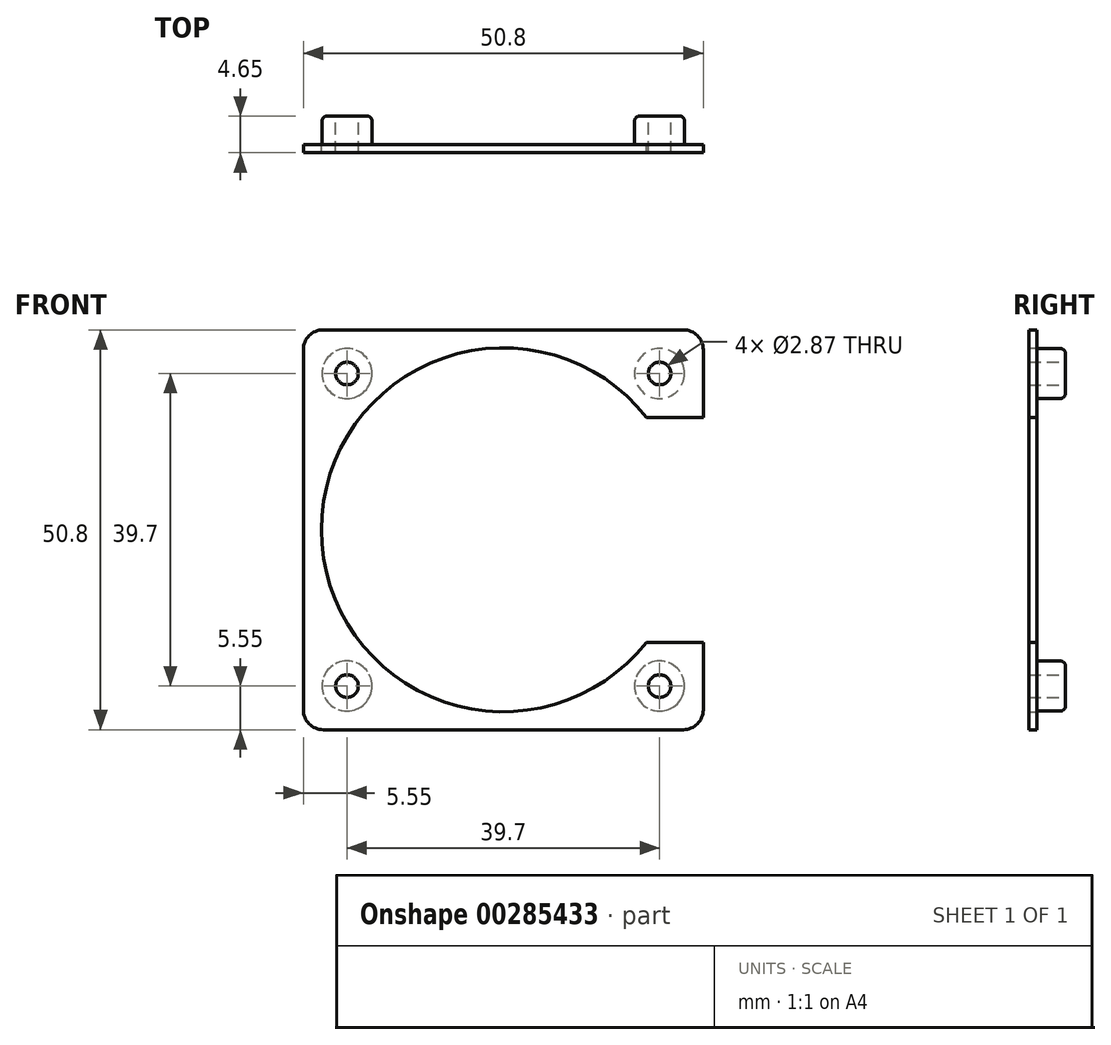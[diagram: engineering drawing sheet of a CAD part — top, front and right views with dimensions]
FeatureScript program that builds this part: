
annotation { "Feature Type Name" : "Feature", "Feature Type Description" : "" }
export const myFeature = defineFeature(function(context is Context, id is Id, definition is map)
    precondition{}
    {
        {
            var Q0;
            Q0=qCreatedBy(makeId("Front.planeOp"),FACE);
            var sketch = newSketch(context, id + "F0", { "sketchPlane" : qUnion([Q0])});
            skLineSegment(sketch, "E0.bottom", {"start": v(2.54, 0) * mm, "end": v(48.26, 0) * mm});
            skLineSegment(sketch, "E0.top", {"start": v(2.54, 50.8) * mm, "end": v(48.26, 50.8) * mm});
            skLineSegment(sketch, "E0.left", {"start": v(0, 2.54) * mm, "end": v(0, 48.26) * mm});
            skLineSegment(sketch, "E0.right", {"start": v(50.8, 2.54) * mm, "end": v(50.8, 11.11) * mm});
            skLineSegment(sketch, "E1", {"start": v(50.8, 39.69) * mm, "end": v(43.57, 39.69) * mm});
            skLineSegment(sketch, "E2", {"start": v(50.8, 11.11) * mm, "end": v(43.57, 11.11) * mm});
            skLineSegment(sketch, "E3", {"start": v(25.4, 50.8) * mm, "end": v(25.4, 0) * mm, "construction": true});
            skLineSegment(sketch, "E4", {"start": v(0, 25.4) * mm, "end": v(50.8, 25.4) * mm, "construction": true});
            skLineSegment(sketch, "E5", {"start": v(43.57, 39.69) * mm, "end": v(43.57, 11.11) * mm, "construction": true});
            skPoint(sketch, "E6", {"position": v(43.57, 25.4) * mm});
            skArc(sketch, "E7", {"start": v(43.57, 39.69) * mm, "mid": v(2.29, 25.4) * mm, "end": v(43.57, 11.11) * mm});
            skLineSegment(sketch, "E8.trimOffspring", {"start": v(50.8, 39.69) * mm, "end": v(50.8, 48.26) * mm});
            skPoint(sketch, "E9.visualSharp", {"position": v(0, 50.8) * mm});
            skArc(sketch, "E9.filletArc", {"start": v(2.54, 50.8) * mm, "mid": v(0.74, 50.06) * mm, "end": v(0, 48.26) * mm});
            skPoint(sketch, "E10.visualSharp", {"position": v(50.8, 50.8) * mm});
            skArc(sketch, "E10.filletArc", {"start": v(50.8, 48.26) * mm, "mid": v(50.06, 50.06) * mm, "end": v(48.26, 50.8) * mm});
            skPoint(sketch, "E11.visualSharp", {"position": v(50.8, 0) * mm});
            skArc(sketch, "E11.filletArc", {"start": v(48.26, 0) * mm, "mid": v(50.06, 0.74) * mm, "end": v(50.8, 2.54) * mm});
            skPoint(sketch, "E12.visualSharp", {"position": v(0, 0) * mm});
            skArc(sketch, "E12.filletArc", {"start": v(0, 2.54) * mm, "mid": v(0.74, 0.74) * mm, "end": v(2.54, 0) * mm});
            skSolve(sketch);
        }
        {
            var Q0;
            Q0 = qSketchRegion(id + "F0", true);
            extrude(context, id + "F1", {"entities" : qUnion([Q0]), "depth" : 1.02 * mm});
        }
        {
            var Q0;
            Q0=makeQuery(id+"F1.opExtrude","CAP_FACE",FACE,{"disambiguationData":[OSD([sQuery(id+"F0.wireOp",EDGE,"E0.bottom"),sQuery(id+"F0.wireOp",EDGE,"E0.top"),sQuery(id+"F0.wireOp",EDGE,"E0.left"),sQuery(id+"F0.wireOp",EDGE,"E0.right"),sQuery(id+"F0.wireOp",EDGE,"E1"),sQuery(id+"F0.wireOp",EDGE,"E2"),sQuery(id+"F0.wireOp",EDGE,"E7"),sQuery(id+"F0.wireOp",EDGE,"E8.trimOffspring"),sQuery(id+"F0.wireOp",EDGE,"E9.filletArc"),sQuery(id+"F0.wireOp",EDGE,"E10.filletArc"),sQuery(id+"F0.wireOp",EDGE,"E11.filletArc"),sQuery(id+"F0.wireOp",EDGE,"E12.filletArc")])],"isStart":true});
            var sketch = newSketch(context, id + "F2", { "sketchPlane" : qUnion([Q0])});
            skCircle(sketch, "E13", {"center": v(-45.25, 45.25) * mm, "radius": 3.18 * mm});
            skLineSegment(sketch, "E14.bottom", {"start": v(-5.55, 45.25) * mm, "end": v(-45.25, 45.25) * mm, "construction": true});
            skLineSegment(sketch, "E14.top", {"start": v(-5.55, 5.55) * mm, "end": v(-45.25, 5.55) * mm, "construction": true});
            skLineSegment(sketch, "E14.left", {"start": v(-5.55, 45.25) * mm, "end": v(-5.55, 5.55) * mm, "construction": true});
            skLineSegment(sketch, "E14.right", {"start": v(-45.25, 45.25) * mm, "end": v(-45.25, 5.55) * mm, "construction": true});
            skLineSegment(sketch, "E15", {"start": v(0, 25.4) * mm, "end": v(-45.25, 25.4) * mm, "construction": true});
            skPoint(sketch, "E15.endSnap0", {"position": v(0, 25.4) * mm});
            skLineSegment(sketch, "E16", {"start": v(-25.4, 50.8) * mm, "end": v(-25.4, 5.55) * mm, "construction": true});
            skCircle(sketch, "E17", {"center": v(-5.55, 45.25) * mm, "radius": 3.18 * mm});
            skCircle(sketch, "E18", {"center": v(-5.55, 5.55) * mm, "radius": 3.18 * mm});
            skCircle(sketch, "E19", {"center": v(-45.25, 5.55) * mm, "radius": 3.18 * mm});
            skSolve(sketch);
        }
        {
            var Q0;
            Q0 = qSketchRegion(id + "F2", true);
            extrude(context, id + "F3", {"entities" : qUnion([Q0]), "operationType" : NewBodyOperationType.ADD, "depth" : 3.63 * mm});
        }
        {
            var Q0;
            Q0=makeQuery(id+"F3.opExtrude","CAP_FACE",FACE,{"disambiguationData":[OSD([sQuery(id+"F2.wireOp",EDGE,"E13")])],"isStart":false});
            var sketch = newSketch(context, id + "F4", { "sketchPlane" : qUnion([Q0])});
            skPoint(sketch, "E20", {"position": v(-45.25, 45.25) * mm});
            skPoint(sketch, "E21", {"position": v(-5.55, 45.25) * mm});
            skPoint(sketch, "E22", {"position": v(-5.55, 5.55) * mm});
            skPoint(sketch, "E23", {"position": v(-45.25, 5.55) * mm});
            skSolve(sketch);
        }
        {
            var Q0;
            Q0=sQuery(id+"F4.wireOp",VERTEX,"E20");
            var Q1;
            Q1=sQuery(id+"F4.wireOp",VERTEX,"E21");
            var Q2;
            Q2=sQuery(id+"F4.wireOp",VERTEX,"E22");
            var Q3;
            Q3=sQuery(id+"F4.wireOp",VERTEX,"E23");
            var Q4;
            Q4=makeQuery(id+"F1.opExtrude","SWEPT_BODY",BODY,{"disambiguationData":[OSD([sQuery(id+"F0.wireOp",EDGE,"E0.bottom"),sQuery(id+"F0.wireOp",EDGE,"E0.top"),sQuery(id+"F0.wireOp",EDGE,"E0.left"),sQuery(id+"F0.wireOp",EDGE,"E0.right"),sQuery(id+"F0.wireOp",EDGE,"E1"),sQuery(id+"F0.wireOp",EDGE,"E2"),sQuery(id+"F0.wireOp",EDGE,"E7"),sQuery(id+"F0.wireOp",EDGE,"E8.trimOffspring"),sQuery(id+"F0.wireOp",EDGE,"E9.filletArc"),sQuery(id+"F0.wireOp",EDGE,"E10.filletArc"),sQuery(id+"F0.wireOp",EDGE,"E11.filletArc"),sQuery(id+"F0.wireOp",EDGE,"E12.filletArc")])]});
            hole(context, id + "F5", {"style" : HoleStyle.SIMPLE, "endStyle" : HoleEndStyle.THROUGH, "standardTappedOrClearance" : lookupTablePath({ "standard" : "ANSI", "engagement" : "75%", "pitch" : "40 tpi", "size" : "#6", "type" : "Tapped" }), "standardBlindInLast" : lookupTablePath({ "standard" : "ANSI", "engagement" : "75%", "pitch" : "40 tpi", "size" : "#6", "type" : "Tapped" }), "holeDiameter" : 2.87 * mm, "showTappedDepth" : true, "isTappedThrough" : true, "tappedDepth" : 2.4 * mm, "tapClearance" : 3, "startFromSketch" : true, "locations" : qUnion([Q0, Q1, Q2, Q3]), "scope" : qUnion([Q4]), "majorDiameter" : 3.5 * mm});
        }
        {
            var Q0;
            Q0=makeQuery(id+"F3.opExtrude","CAP_EDGE",EDGE,{"disambiguationData":[OSD([sQuery(id+"F2.wireOp",EDGE,"E13")])],"isStart":false});
            var Q1;
            Q1=makeQuery(id+"F3.opExtrude","CAP_EDGE",EDGE,{"disambiguationData":[OSD([sQuery(id+"F2.wireOp",EDGE,"E17")])],"isStart":false});
            var Q2;
            Q2=makeQuery(id+"F3.opExtrude","CAP_EDGE",EDGE,{"disambiguationData":[OSD([sQuery(id+"F2.wireOp",EDGE,"E18")])],"isStart":false});
            var Q3;
            Q3=makeQuery(id+"F3.opExtrude","CAP_EDGE",EDGE,{"disambiguationData":[OSD([sQuery(id+"F2.wireOp",EDGE,"E19")])],"isStart":false});
            fillet(context, id + "F6", {"entities" : qUnion([Q0, Q1, Q2, Q3]), "radius" : 0.64 * mm, "tangentPropagation" : true, "allowEdgeOverflow" : false});
        }
    });
